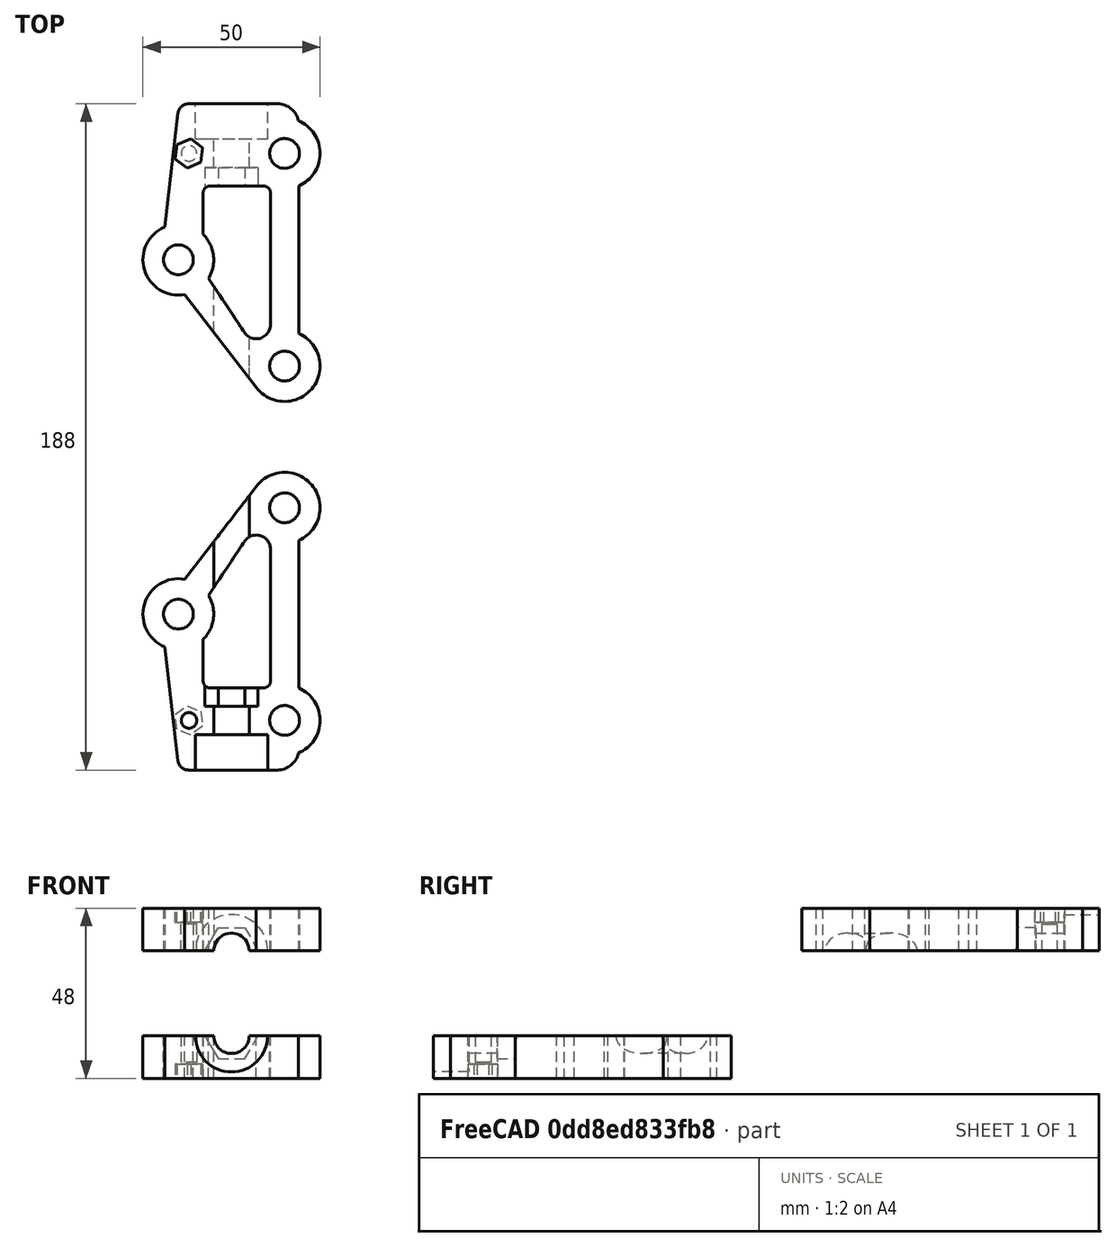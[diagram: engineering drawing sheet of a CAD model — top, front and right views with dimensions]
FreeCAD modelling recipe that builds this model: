
FCSTD DOCUMENT  (FreeCAD 0.15R4664 (Git))
Label: y_nut_holder_B
License: All rights reserved
LicenseURL: http://en.wikipedia.org/wiki/All_rights_reserved
objects: Part::Cylinder×9, Part::Cut×7, Part::Fillet×4, Part::Feature×3, Part::MultiFuse×3, Part::Prism×2, Part::Chamfer×2, Part::Box×1, Part::Mirroring×1
note: 32 computed .brp shape members not serialized (recipe doc carries the construction recipe); baked Part::Feature solids carry a one-line shape summary decoded from their .brp

FEATURE [Part::Box] Box  label="Cubo"
  Height = 12
  Length = 39
  Placement = pos=(5,14,0) rot=(0,0,1;0rad)
  Width = 80
FEATURE [Part::Cylinder] Cylinder  label="Cilindro"
  Angle = 360
  Height = 12
  Placement = pos=(40,20,0) rot=(0,0,1;0rad)
  Radius = 10
FEATURE [Part::Cylinder] Cylinder001  label="Cilindro001"
  Angle = 360
  Height = 12
  Placement = pos=(10,50,0) rot=(0,0,1;0rad)
  Radius = 10
FEATURE [Part::Cylinder] Cylinder002  label="Cilindro002"
  Angle = 360
  Height = 12
  Placement = pos=(40,80,0) rot=(0,0,1;0rad)
  Radius = 10
FEATURE [Part::Prism] Prism  label="Prisma"
  Circumradius = 4.2
  Height = 4
  Placement = pos=(13,80,-4) rot=(0,0,1;1.44862rad)
  Polygon = 6
FEATURE [Part::Cylinder] Cylinder007  label="screw_hole_2"
  Angle = 360
  Height = 14.5
  Placement = pos=(13,80,-19) rot=(0,0,1;0rad)
  Radius = 2.2
FEATURE [Part::Feature] YnutholderL001001  label="YnutholderL002"
  Placement = pos=(50,10,0) rot=(0,0,1;1.5708rad)
  shape: bbox 50 x 84 x 12 mm, 1642 faces, 0 solids (baked)
FEATURE [Part::MultiFuse] Fusion
  Shapes = -> [Cylinder001,Cylinder,Cylinder002]
FEATURE [Part::Chamfer] Chamfer
  Base = -> Box
  Edges = 1 edges: [Edge1 r1=35 r2=27]
FEATURE [Part::Chamfer] Chamfer001
  Base = -> Chamfer
  Edges = 1 edges: [Edge3 r1=44.9 r2=5.2]
FEATURE [Part::Fillet] Fillet
  Base = -> Chamfer001
  Edges = 1 edges r=3: [Edge11]
FEATURE [Part::Fillet] Fillet001
  Base = -> Fillet
  Edges = 1 edges r=6: [Edge16]
FEATURE [Part::Cylinder] Cylinder009  label="Cilindro003"
  Angle = 360
  Height = 14
  Placement = pos=(40,20,-1) rot=(0,0,1;0rad)
  Radius = 4.2
FEATURE [Part::Cylinder] Cylinder010  label="Cilindro004"
  Angle = 360
  Height = 14
  Placement = pos=(40,80,-1) rot=(0,0,1;0rad)
  Radius = 4.2
FEATURE [Part::Cylinder] Cylinder011  label="Cilindro005"
  Angle = 360
  Height = 14
  Placement = pos=(10,50,-1) rot=(0,0,1;0rad)
  Radius = 4.2
FEATURE [Part::MultiFuse] Fusion004
  Shapes = -> [Cylinder009,Cylinder010,Cylinder011]
FEATURE [Part::Feature] Pad001
  Placement = pos=(50,10,-1) rot=(0,0,1;1.5708rad)
  shape: bbox 19 x 52.4 x 14 mm, 6 faces (baked)
FEATURE [Part::Cut] Cut
  Base = -> Fillet001
  Tool = -> Pad001
FEATURE [Part::Fillet] Fillet002
  Base = -> Cut
  Edges = 2 edges r=2: [Edge31,Edge33]
FEATURE [Part::Fillet] Fillet003
  Base = -> Fillet002
  Edges = 1 edges r=4: [Edge17]
FEATURE [Part::MultiFuse] Fusion005
  Shapes = -> [Fillet003,Fusion]
FEATURE [Part::Cut] Cut001
  Base = -> Fusion005
  Tool = -> Fusion004
FEATURE [Part::Cylinder] Cylinder012  label="Cilindro006"
  Angle = 360
  Height = 80
  Placement = pos=(25,15,12) rot=(-1,0,0;1.5708rad)
  Radius = 5
FEATURE [Part::Cut] Cut002
  Base = -> Cut001
  Tool = -> Cylinder012
FEATURE [Part::Prism] Prism001  label="Prisma001"
  Circumradius = 7.5
  Height = 7
  Placement = pos=(25,76,12) rot=(1,0,0;1.5708rad)
  Polygon = 6
FEATURE [Part::Cut] Cut003
  Base = -> Cut002
  Tool = -> Prism001
FEATURE [Part::Cylinder] Cylinder013  label="Cilindro007"
  Angle = 360
  Height = 11
  Placement = pos=(25,84,12) rot=(-1,0,0;1.5708rad)
  Radius = 10.2
FEATURE [Part::Cut] Cut004
  Base = -> Cut003
  Tool = -> Cylinder013
FEATURE [Part::Mirroring] Part__Mirroring  label="Cut004 (Mirror #1)"
  Base = (0,0,0)
  Normal = (0,0,1)
  Source = -> Cut004
FEATURE [Part::Cut] Cut005
  Base = -> Part__Mirroring
  Tool = -> Prism
FEATURE [Part::Cut] Cut006  label="y_nut_holder_B"
  Base = -> Cut005
  Placement = pos=(0,0,24) rot=(0,0,1;0rad)
  Tool = -> Cylinder007
FEATURE [Part::Feature] Cut006_solid  label="y_nut_holder_B (Solid)"
  Placement = pos=(0,0,0) rot=(1,0,0;3.14159rad)
  shape: bbox 50 x 84 x 12 mm, 40 faces (baked)
